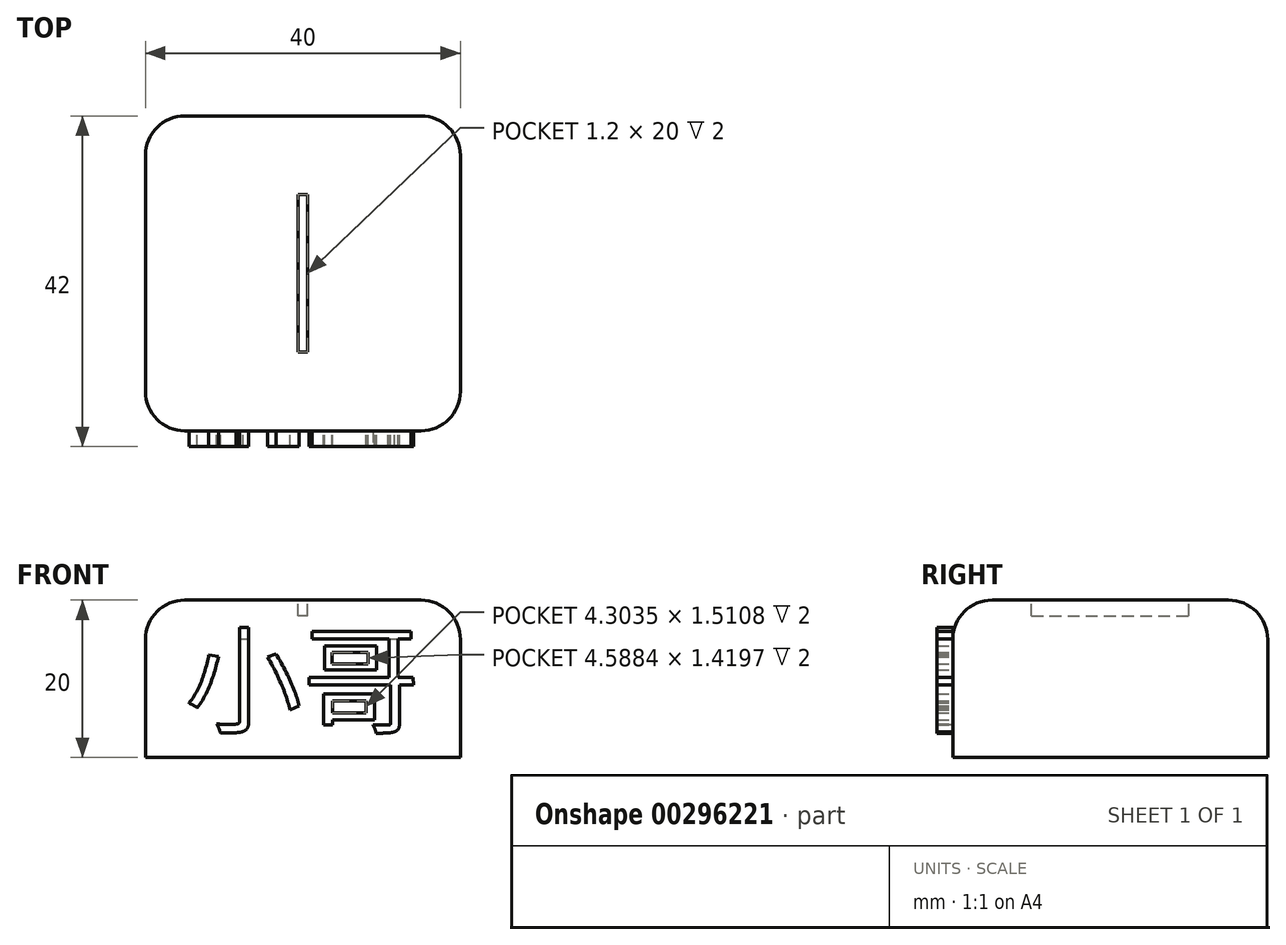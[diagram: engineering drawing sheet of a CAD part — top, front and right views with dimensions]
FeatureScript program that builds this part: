
annotation { "Feature Type Name" : "Feature", "Feature Type Description" : "" }
export const myFeature = defineFeature(function(context is Context, id is Id, definition is map)
    precondition{}
    {
        {
            var Q0;
            Q0=qCreatedBy(makeId("Top.planeOp"),FACE);
            var sketch = newSketch(context, id + "F0", { "sketchPlane" : qUnion([Q0])});
            skLineSegment(sketch, "E0.bottom", {"start": v(20, -20) * mm, "end": v(-20, -20) * mm});
            skLineSegment(sketch, "E0.top", {"start": v(20, 20) * mm, "end": v(-20, 20) * mm});
            skLineSegment(sketch, "E0.left", {"start": v(20, -20) * mm, "end": v(20, 20) * mm});
            skLineSegment(sketch, "E0.right", {"start": v(-20, -20) * mm, "end": v(-20, 20) * mm});
            skPoint(sketch, "E0.middle", {"position": v(0, 0) * mm});
            skLineSegment(sketch, "E1.bottom", {"start": v(0.6, -10) * mm, "end": v(-0.6, -10) * mm});
            skLineSegment(sketch, "E1.top", {"start": v(0.6, 10) * mm, "end": v(-0.6, 10) * mm});
            skLineSegment(sketch, "E1.left", {"start": v(0.6, -10) * mm, "end": v(0.6, 10) * mm});
            skLineSegment(sketch, "E1.right", {"start": v(-0.6, -10) * mm, "end": v(-0.6, 10) * mm});
            skSolve(sketch);
        }
        {
            var Q0;
            Q0=makeQuery(id+"F0.imprint","IMPRINT",FACE,{"disambiguationData":[TD([[makeQuery(id+"F0.imprint","IMPRINT",EDGE,{"derivedFrom":sQuery(id+"F0.wireOp",EDGE,"E0.bottom")}),-1.0]])]});
            var Q1;
            Q1=makeQuery(id+"F0.imprint","IMPRINT",FACE,{"disambiguationData":[TD([[makeQuery(id+"F0.imprint","IMPRINT",EDGE,{"derivedFrom":sQuery(id+"F0.wireOp",EDGE,"E1.bottom")}),-1.0]])]});
            extrude(context, id + "F1", {"entities" : qUnion([Q0, Q1]), "oppositeDirection" : true, "depth" : 20 * mm});
        }
        {
            var Q0;
            Q0=makeQuery(id+"F0.imprint","IMPRINT",FACE,{"disambiguationData":[TD([[makeQuery(id+"F0.imprint","IMPRINT",EDGE,{"derivedFrom":sQuery(id+"F0.wireOp",EDGE,"E1.bottom")}),-1.0]])]});
            extrude(context, id + "F2", {"entities" : qUnion([Q0]), "operationType" : NewBodyOperationType.REMOVE, "oppositeDirection" : true, "depth" : 2 * mm});
        }
        {
            var Q0;
            Q0=makeQuery(id+"F2.boolean.opBoolean","COPY",EDGE,{"derivedFrom":makeQuery(id+"F2.opExtrude","CAP_EDGE",EDGE,{"disambiguationData":[OSD([sQuery(id+"F0.wireOp",EDGE,"E1.left")])],"isStart":true})});
            var Q1;
            Q1=makeQuery(id+"F2.boolean.opBoolean","COPY",EDGE,{"derivedFrom":makeQuery(id+"F2.opExtrude","CAP_EDGE",EDGE,{"disambiguationData":[OSD([sQuery(id+"F0.wireOp",EDGE,"E1.right")])],"isStart":true})});
            var Q2;
            Q2=makeQuery(id+"F1.opExtrude","SWEPT_EDGE",EDGE,{"disambiguationData":[OSD([sQuery(id+"F0.wireOp",EDGE,"E0.bottom"),sQuery(id+"F0.wireOp",EDGE,"E0.left")])]});
            var Q3;
            Q3=makeQuery(id+"F1.opExtrude","SWEPT_EDGE",EDGE,{"disambiguationData":[OSD([sQuery(id+"F0.wireOp",EDGE,"E0.top"),sQuery(id+"F0.wireOp",EDGE,"E0.left")])]});
            var Q4;
            Q4=makeQuery(id+"F1.opExtrude","CAP_EDGE",EDGE,{"disambiguationData":[OSD([sQuery(id+"F0.wireOp",EDGE,"E0.left")])],"isStart":true});
            var Q5;
            Q5=makeQuery(id+"F1.opExtrude","SWEPT_EDGE",EDGE,{"disambiguationData":[OSD([sQuery(id+"F0.wireOp",EDGE,"E0.bottom"),sQuery(id+"F0.wireOp",EDGE,"E0.right")])]});
            var Q6;
            Q6=makeQuery(id+"F1.opExtrude","SWEPT_EDGE",EDGE,{"disambiguationData":[OSD([sQuery(id+"F0.wireOp",EDGE,"E0.top"),sQuery(id+"F0.wireOp",EDGE,"E0.right")])]});
            var Q7;
            Q7=makeQuery(id+"F1.opExtrude","CAP_EDGE",EDGE,{"disambiguationData":[OSD([sQuery(id+"F0.wireOp",EDGE,"E0.top")])],"isStart":true});
            var Q8;
            Q8=makeQuery(id+"F1.opExtrude","CAP_EDGE",EDGE,{"disambiguationData":[OSD([sQuery(id+"F0.wireOp",EDGE,"E0.right")])],"isStart":true});
            var Q9;
            Q9=makeQuery(id+"F1.opExtrude","CAP_EDGE",EDGE,{"disambiguationData":[OSD([sQuery(id+"F0.wireOp",EDGE,"E0.bottom")])],"isStart":true});
            fillet(context, id + "F3", {"entities" : qUnion([Q0, Q1, Q2, Q3, Q4, Q5, Q6, Q7, Q8, Q9]), "radius" : 5 * mm, "tangentPropagation" : true, "allowEdgeOverflow" : false});
        }
        {
            var Q0;
            Q0=makeQuery(id+"F1.opExtrude","SWEPT_FACE",FACE,{"disambiguationData":[OSD([sQuery(id+"F0.wireOp",EDGE,"E0.bottom")])]});
            var sketch = newSketch(context, id + "F4", { "sketchPlane" : qUnion([Q0])});
            skText(sketch, "E2", { "text": "小哥", "fontName": "NotoSansCJKtc-Regular.otf"});
            const initialGuessF4  = {"E2": [-0.015, -0.01576, 1, 0, 0.01076]};
            skSetInitialGuess(sketch, initialGuessF4);
            skSolve(sketch);
        }
        {
            var Q0;
            Q0=qSketchRegion(id+"F4",true);
            extrude(context, id + "F5", {"entities" : qUnion([Q0]), "operationType" : NewBodyOperationType.ADD, "depth" : 2 * mm});
        }
    });
